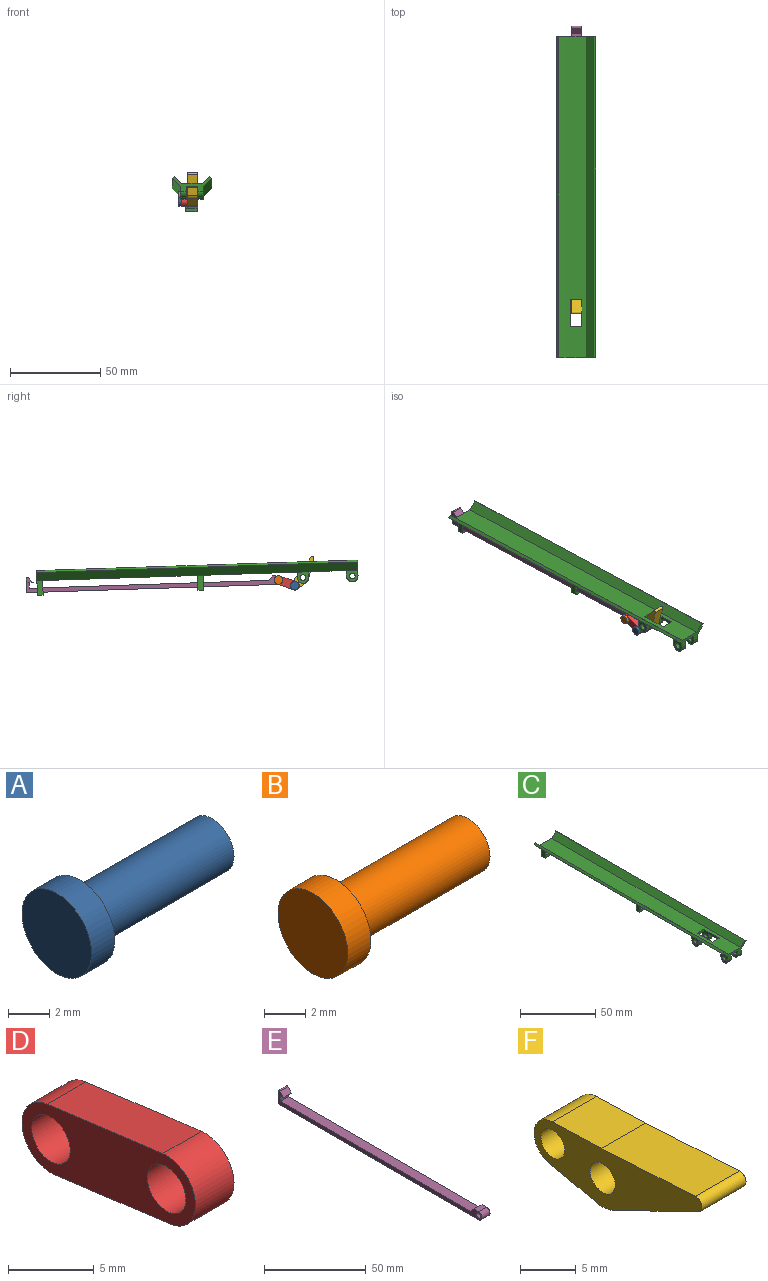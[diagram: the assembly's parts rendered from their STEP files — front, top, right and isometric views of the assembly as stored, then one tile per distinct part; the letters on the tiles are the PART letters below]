
ASSEMBLY  parts=6 mates=6
PART A: 5 faces, bbox 10.6x4.8x4.8 mm
  f0: plane 3x3mm, normal (1,0,0), area 7.1mm2, adj f1
  f1: cylinder r=1.5mm len=9.04mm, axis (-1,0,0), area 85.1mm2, adj f0,f4
  f2: cylinder r=2.38mm len=4.76mm, axis (1,0,0), area 23.8mm2, adj f3,f4
  f3: plane 4.76x4.76mm, normal (-1,0,0), area 17.8mm2, adj f2
  f4: plane 4.76x4.76mm, normal (1,0,0), area 10.8mm2, adj f1,f2
PART B: 5 faces, bbox 10.6x4.8x4.8 mm
  f0: plane 3x3mm, normal (1,0,0), area 7.1mm2, adj f1
  f1: cylinder r=1.5mm len=9.02mm, axis (-1,0,0), area 84.9mm2, adj f0,f4
  f2: cylinder r=2.38mm len=4.76mm, axis (1,0,0), area 23.8mm2, adj f3,f4
  f3: plane 4.76x4.76mm, normal (-1,0,0), area 17.8mm2, adj f2
  f4: plane 4.76x4.76mm, normal (1,0,0), area 10.8mm2, adj f1,f2
PART C: 52 faces, bbox 21.7x177.8x13.9 mm
  f0: plane 3.18x3.18mm, normal (0,1,0), area 10.1mm2, adj f3,f4,f49,f50
  f1: plane 21.68x8.79mm, normal (0,-1,0), area 58.4mm2, adj f3,f4,f10,f11,f12,f13,f14,f15
  f2: cylinder r=1.59mm len=3.18mm, axis (-1,0,0), area 31.7mm2, adj f49,f50
  f3: cylinder r=3.17mm len=6.35mm, axis (-1,0,0), area 31.7mm2, adj f0,f1,f49,f50
  f4: plane 27.31x12.7mm, normal (0,0,-1), area 244.4mm2, adj f0,f1,f5,f13,f14,f18,f20,f21
  f5: plane 3.18x3.18mm, normal (0,-1,0), area 10.1mm2, adj f4,f7,f20,f27
  f6: plane 3.18x3.18mm, normal (0,1,0), area 10.1mm2, adj f7,f9,f20,f27
  f7: cylinder r=3.17mm len=6.35mm, axis (-1,0,0), area 31.7mm2, adj f5,f6,f20,f27
  f8: cylinder r=1.59mm len=3.18mm, axis (-1,0,0), area 31.7mm2, adj f20,f27
  f9: plane 145.8x12.7mm, normal (0,0,-1), area 1800.8mm2, adj f6,f13,f14,f17,f18,f19,f20,f24
  f10: plane 177.8x11.39mm, normal (0,0,1), area 1932.3mm2, adj f1,f11,f16,f17,f18,f19,f20,f21
  f11: plane 177.8x4.03mm, normal (0.71,0,0.71), area 1012.1mm2, adj f1,f10,f12,f17
  f12: plane 177.8x1.12mm, normal (-0.71,0,0.71), area 282.3mm2, adj f1,f11,f13,f17
  f13: plane 177.8x4.49mm, normal (-0.71,0,-0.71), area 1129mm2, adj f1,f4,f9,f12,f17,f27,f49
  f14: plane 177.8x4.49mm, normal (0.71,0,-0.71), area 1129mm2, adj f1,f4,f9,f15,f17,f26,f48
  f15: plane 177.8x1.12mm, normal (0.71,0,0.71), area 282.3mm2, adj f1,f14,f16,f17
  f16: plane 177.8x4.03mm, normal (-0.71,0,0.71), area 1012.1mm2, adj f1,f10,f15,f17
  f17: plane 21.68x13.86mm, normal (0,1,0), area 72mm2, adj f9,f10,f11,f12,f13,f14,f15,f16
  f18: plane 16.13x7.94mm, normal (-1,0,0), area 51.1mm2, adj f4,f9,f10,f19,f21,f22,f23,f24
  f19: plane 6.35x1.59mm, normal (0,-1,0), area 10.1mm2, adj f9,f10,f18,f20
  f20: plane 16.13x7.94mm, normal (1,0,0), area 51.1mm2, adj f4,f5,f6,f7,f8,f9,f10,f19
  f21: plane 6.35x1.59mm, normal (0,1,0), area 10.1mm2, adj f4,f10,f18,f20
  f22: plane 3.18x3.18mm, normal (0,-1,0), area 10.1mm2, adj f4,f18,f23,f26
  f23: cylinder r=3.17mm len=6.35mm, axis (-1,0,0), area 31.7mm2, adj f18,f22,f24,f26
  f24: plane 3.18x3.18mm, normal (0,1,0), area 10.1mm2, adj f9,f18,f23,f26
  f25: cylinder r=1.59mm len=3.18mm, axis (-1,0,0), area 31.7mm2, adj f18,f26
  f26: plane 6.35x6.35mm, normal (1,0,0), area 28.1mm2, adj f14,f22,f23,f24,f25
  f27: plane 6.35x6.35mm, normal (-1,0,0), area 28.1mm2, adj f5,f6,f7,f8,f13
  f28: plane 3.18x3.18mm, normal (1,0,0), area 10.1mm2, adj f9,f34,f35,f36
  f29: plane 8.24x3.18mm, normal (-1,0,0), area 26.2mm2, adj f9,f30,f35,f36
  f30: plane 6.35x3.18mm, normal (0,0,-1), area 20.2mm2, adj f29,f31,f35,f36
  f31: plane 3.18x1.82mm, normal (1,0,0), area 5.8mm2, adj f30,f32,f35,f36
  f32: plane 5.72x3.18mm, normal (0,0,1), area 18.1mm2, adj f31,f33,f35,f36
  f33: plane 3.25x3.18mm, normal (1,0,0), area 10.3mm2, adj f32,f34,f35,f36
  f34: plane 5.72x3.18mm, normal (0,0,-1), area 18.1mm2, adj f28,f33,f35,f36
  f35: plane 8.24x6.35mm, normal (0,-1,0), area 33.8mm2, adj f9,f28,f29,f30,f31,f32,f33,f34
  f36: plane 8.24x6.35mm, normal (0,1,0), area 33.8mm2, adj f9,f28,f29,f30,f31,f32,f33,f34
  f37: plane 8.24x3.18mm, normal (-1,0,0), area 26.2mm2, adj f9,f17,f43,f44
  f38: plane 3.18x3.18mm, normal (1,0,0), area 10.1mm2, adj f9,f17,f39,f44
  f39: plane 5.72x3.18mm, normal (0,0,-1), area 18.1mm2, adj f17,f38,f40,f44
  f40: plane 3.25x3.18mm, normal (1,0,0), area 10.3mm2, adj f17,f39,f41,f44
  f41: plane 5.72x3.18mm, normal (0,0,1), area 18.1mm2, adj f17,f40,f42,f44
  f42: plane 3.18x1.82mm, normal (1,0,0), area 5.8mm2, adj f17,f41,f43,f44
  f43: plane 6.35x3.18mm, normal (0,0,-1), area 20.2mm2, adj f17,f37,f42,f44
  f44: plane 8.24x6.35mm, normal (0,-1,0), area 33.8mm2, adj f9,f37,f38,f39,f40,f41,f42,f43
  f45: plane 3.18x3.18mm, normal (0,1,0), area 10.1mm2, adj f4,f47,f48,f51
  f46: cylinder r=1.59mm len=3.18mm, axis (-1,0,0), area 31.7mm2, adj f48,f51
  f47: cylinder r=3.17mm len=6.35mm, axis (-1,0,0), area 31.7mm2, adj f1,f45,f48,f51
  f48: plane 6.35x6.35mm, normal (1,0,0), area 28.1mm2, adj f1,f14,f45,f46,f47
  f49: plane 6.35x6.35mm, normal (-1,0,0), area 28.1mm2, adj f0,f1,f2,f3,f13
  f50: plane 6.35x6.35mm, normal (1,0,0), area 28.1mm2, adj f0,f1,f2,f3,f4
  f51: plane 6.35x6.35mm, normal (-1,0,0), area 28.1mm2, adj f1,f4,f45,f46,f47
PART D: 8 faces, bbox 3.2x14.3x6 mm
  f0: plane 9.53x3.18mm, normal (0,-0.13,-0.99), area 30.5mm2, adj f1,f3,f4,f5
  f1: cylinder r=2.38mm len=4.74mm, axis (1,0,0), area 23.8mm2, adj f0,f2,f4,f5
  f2: plane 9.53x3.18mm, normal (0,0.13,0.99), area 30.5mm2, adj f1,f3,f4,f5
  f3: cylinder r=2.38mm len=4.74mm, axis (1,0,0), area 23.8mm2, adj f0,f2,f4,f5
  f4: plane 14.29x6mm, normal (-1,0,0), area 47.7mm2, adj f0,f1,f2,f3,f6,f7
  f5: plane 14.29x6mm, normal (1,0,0), area 47.7mm2, adj f0,f1,f2,f3,f6,f7
  f6: cylinder r=1.59mm len=3.18mm, axis (-1,0,0), area 31.7mm2, adj f4,f5
  f7: cylinder r=1.59mm len=3.18mm, axis (-1,0,0), area 31.7mm2, adj f4,f5
PART E: 13 faces, bbox 5.6x142.1x8.4 mm
  f0: plane 5.59x2.25mm, normal (0,0,-1), area 12.6mm2, adj f1,f10,f11,f12
  f1: plane 5.59x3.3mm, normal (0,-1,0), area 18.5mm2, adj f0,f2,f11,f12
  f2: plane 132.78x5.59mm, normal (0,0,1), area 742mm2, adj f1,f3,f11,f12
  f3: plane 5.59x2.38mm, normal (0,0.74,0.67), area 17.9mm2, adj f2,f4,f11,f12
  f4: plane 5.59x3.19mm, normal (0,0,1), area 17.8mm2, adj f3,f5,f11,f12
  f5: cylinder r=2.38mm len=5.59mm, axis (-1,0,0), area 41.8mm2, adj f4,f6,f11,f12
  f6: plane 139.7x5.59mm, normal (0,0,-1), area 780.6mm2, adj f5,f7,f11,f12
  f7: plane 7.61x5.59mm, normal (0,1,0), area 42.5mm2, adj f6,f8,f11,f12
  f8: cylinder r=0.79mm len=5.59mm, axis (-1,0,0), area 10.4mm2, adj f7,f10,f11,f12
  f9: cylinder r=1.5mm len=5.59mm, axis (-1,0,0), area 52.6mm2, adj f11,f12
  f10: plane 5.59x2.49mm, normal (0,-0.71,0.71), area 19.7mm2, adj f0,f8,f11,f12
  f11: plane 142.08x8.4mm, normal (1,0,0), area 356.5mm2, adj f0,f1,f2,f3,f4,f5,f6,f7
  f12: plane 142.08x8.4mm, normal (-1,0,0), area 356.5mm2, adj f0,f1,f2,f3,f4,f5,f6,f7
PART F: 11 faces, bbox 5.6x21.3x7 mm
  f0: plane 6.15x5.59mm, normal (0,0.22,-0.98), area 35.2mm2, adj f1,f8,f9,f10
  f1: cylinder r=2.38mm len=5.59mm, axis (-1,0,0), area 38.5mm2, adj f0,f2,f9,f10
  f2: plane 6.25x5.59mm, normal (0,0.03,1), area 35mm2, adj f1,f3,f9,f10
  f3: plane 11.89x5.59mm, normal (0,0.06,1), area 66.6mm2, adj f2,f4,f9,f10
  f4: cylinder r=0.79mm len=5.59mm, axis (-1,0,0), area 12.2mm2, adj f3,f5,f9,f10
  f5: plane 10.76x5.59mm, normal (0,-0.44,-0.9), area 66.8mm2, adj f4,f8,f9,f10
  f6: cylinder r=1.59mm len=5.59mm, axis (-1,0,0), area 55.7mm2, adj f9,f10
  f7: cylinder r=1.5mm len=5.59mm, axis (-1,0,0), area 52.6mm2, adj f9,f10
  f8: cylinder r=3.17mm len=5.59mm, axis (-1,0,0), area 11.9mm2, adj f0,f5,f9,f10
  f9: plane 21.29x7.05mm, normal (1,0,0), area 79.8mm2, adj f0,f1,f2,f3,f4,f5,f6,f7
  f10: plane 21.29x7.05mm, normal (-1,0,0), area 79.8mm2, adj f0,f1,f2,f3,f4,f5,f6,f7
PLACE A rot(axis=(1,0,0),6.3deg) t=(-1.85,-17.1,13.2)mm
PLACE B rot(axis=(1,0,0),102.5deg) t=(-1.87,-72.47,48.79)mm
PLACE C rot(axis=(-1,0,0),1.9deg) t=(-2.23,-14.62,10.61)mm fixed
PLACE D rot(axis=(1,0,0),26.5deg) t=(-2.13,-23.13,30.47)mm
PLACE E rot(axis=(-1,0,0),1.9deg) t=(-1.87,-16.84,10.46)mm
PLACE F rot(axis=(-1,0,0),50deg) t=(-1.85,-33.14,-33.35)mm
MATE revolute F.f6 <-> C.f7  axis (-1,0,0) through (0.95,-73.11,9.37)mm
MATE revolute B.f1 <-> D.f3  axis (-1,0,0) through (-8.1,-59.52,8.05)mm
MATE revolute D.f1 <-> A.f1  axis (-1,0,0) through (-8.1,-68.59,4.91)mm
MATE planar E.f6 <-> C.f41  axis (0,-0.03,-1) through (-1.87,10.21,3.36)mm
MATE revolute A.f1 <-> F.f1  axis (-1,0,0) through (0.95,-68.59,4.91)mm
MATE revolute B.f1 <-> E.f5  axis (-1,0,0) through (0.92,-59.52,8.05)mm
